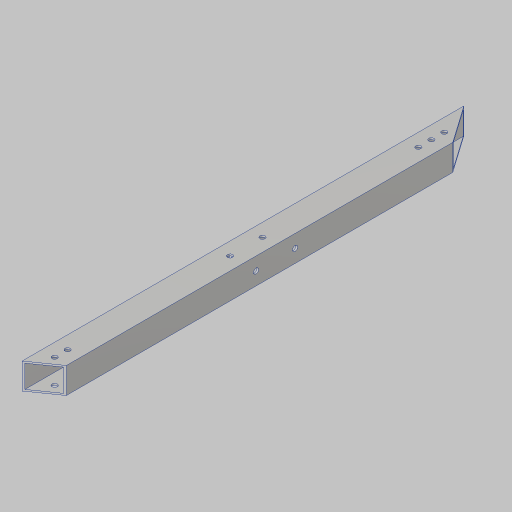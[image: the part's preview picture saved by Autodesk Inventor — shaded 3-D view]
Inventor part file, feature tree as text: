
AUTODESK INVENTOR PART (.ipt)
format: ipt  version: 2023.5 (Build 275446000, 446)  size: 156,672 bytes
history: native  units: in
note: dims shown in document units (in); Inventor stores cm internally (conversion verified against a paired STEP export)
features: sketch x4, hole x3, extrude x2, projected_geometry x2
ambient origin geometry x8: Origin, YZ Plane, XZ Plane, XY Plane, X Axis, Y Axis, Z Axis, Center Point
bodies: Solid1 (feature_tree)
feature tree (11):
  extrude  "Extrusion1"  TaperAngle=0.0deg  [1 undecoded]
  extrude  "Extrusion3"  Depth=0.75in
  hole  "Hole1"  [1 undecoded]
  hole  "Hole2"  [1 undecoded]
  hole  "Hole3"  [1 undecoded]
  sketch  "Sketch3"  dims[d4=0.0in d10=0.0in d11=0.0in]
  projected_geometry  "Projected Loop1"
  sketch  "Sketch4"  dims[d12=0.3779in d13=0.75in]
  sketch  "Sketch5"  dims[d14=1.5748in d16=0.5in d17=0.3937in d19=1.0in]
  sketch  "Sketch6"  dims[d21=0.201in d22=0.38in d23=0.385in d24=0.25in d25=0.5635in d26=1.0in d27=0.8108in d28=1.25in d29=1.1811in d31=0.5in d32=0.3937in d34=1.0in d36=1.5in d37=7.5in d38=0.201in d39=0.38in d40=0.385in d41=0.25in d42=0.5635in d43=1.0in d44=0.8108in d45=1.25in d46=0.5in d47=6.0in d48=0.201in d49=0.75in d50=0.375in d51=0.19in d52=0.5635in d53=0.375in d54=0.0in]
  projected_geometry  "Project Cut Edges1"
note: 4 required parameter values undecoded (feature->parameter linkage not recoverable at this tier; creation-order binding heuristic only, values carry confidence <= 0.55)
